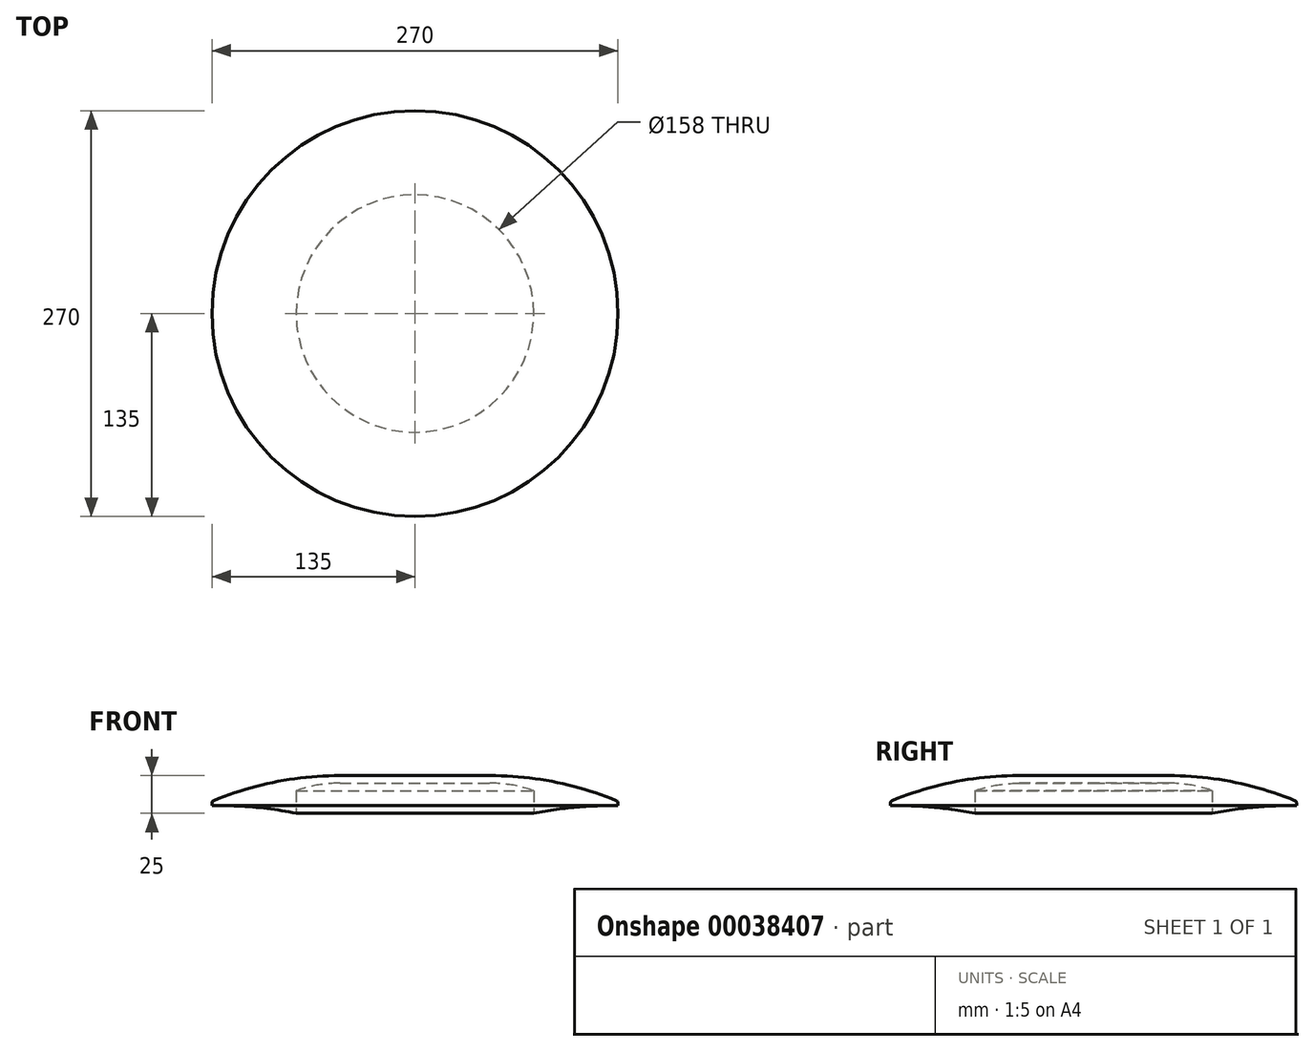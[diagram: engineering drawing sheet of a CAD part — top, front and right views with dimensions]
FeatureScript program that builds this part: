
annotation { "Feature Type Name" : "Feature", "Feature Type Description" : "" }
export const myFeature = defineFeature(function(context is Context, id is Id, definition is map)
    precondition{}
    {
        {
            var Q0;
            Q0=qCreatedBy(makeId("Right.planeOp"),FACE);
            var sketch = newSketch(context, id + "F0", { "sketchPlane" : qUnion([Q0])});
            skLineSegment(sketch, "E0", {"start": v(0, 0) * mm, "end": v(50, 0) * mm});
            skLineSegment(sketch, "E1", {"start": v(0, -5) * mm, "end": v(50, -5) * mm});
            skArc(sketch, "E2", {"start": v(135, -17) * mm, "mid": v(93.34, -4.3) * mm, "end": v(50, 0) * mm});
            skArc(sketch, "E3", {"start": v(79, -10) * mm, "mid": v(64.71, -6.26) * mm, "end": v(50, -5) * mm});
            skLineSegment(sketch, "E4", {"start": v(79, -10) * mm, "end": v(79, -25) * mm});
            skLineSegment(sketch, "E5", {"start": v(135, -20) * mm, "end": v(135, -17) * mm});
            skLineSegment(sketch, "E6", {"start": v(0, -5) * mm, "end": v(0, 0) * mm});
            skArc(sketch, "E7", {"start": v(135, -20) * mm, "mid": v(106.86, -20.92) * mm, "end": v(79, -25) * mm});
            skSolve(sketch);
        }
        {
            var Q0;
            Q0=makeQuery(id+"F0.imprint","IMPRINT",FACE,{"disambiguationData":[TD([[makeQuery(id+"F0.imprint","IMPRINT",EDGE,{"derivedFrom":sQuery(id+"F0.wireOp",EDGE,"E0")}),-1.0]])]});
            var Q1;
            Q1=sQuery(id+"F0.wireOp",EDGE,"E6");
            revolve(context, id + "F1", {"entities" : qUnion([Q0]), "axis" : qUnion([Q1]), "revolveType" : RevolveType.FULL});
        }
        {
            var Q0;
            Q0=makeQuery(id+"F1.opRevolve","SWEPT_EDGE",EDGE,{"disambiguationData":[OSD([sQuery(id+"F0.wireOp",EDGE,"E2"),sQuery(id+"F0.wireOp",EDGE,"E5")])]});
            fillet(context, id + "F2", {"entities" : qUnion([Q0]), "radius" : 1.6 * mm, "tangentPropagation" : true, "allowEdgeOverflow" : false});
        }
    });
